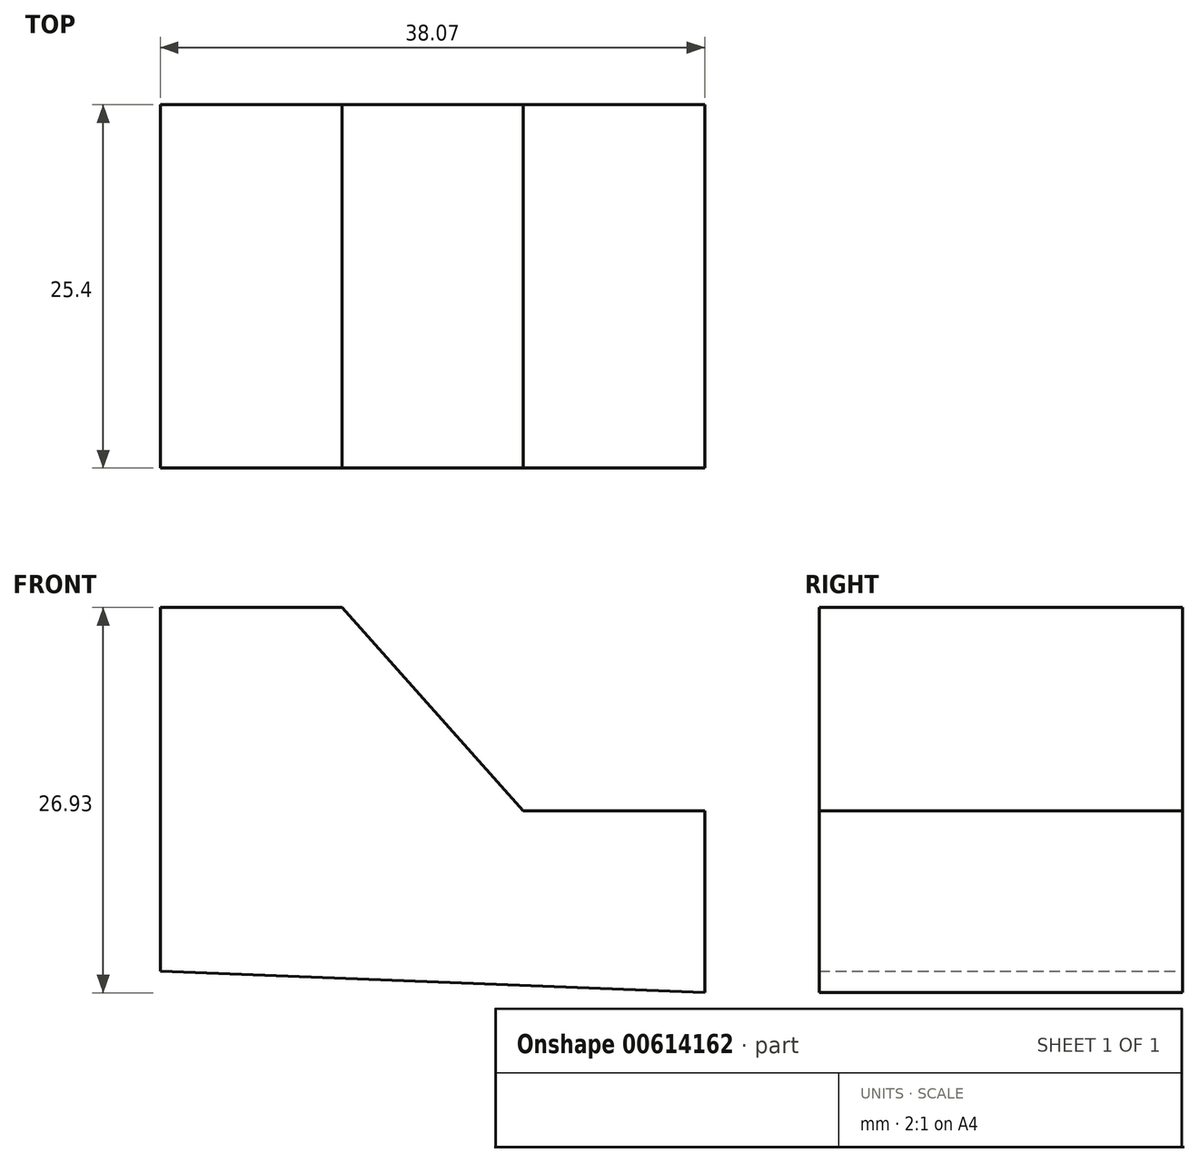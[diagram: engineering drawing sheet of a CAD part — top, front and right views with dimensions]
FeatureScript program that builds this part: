
annotation { "Feature Type Name" : "Feature", "Feature Type Description" : "" }
export const myFeature = defineFeature(function(context is Context, id is Id, definition is map)
    precondition{}
    {
        {
            var Q0;
            Q0=qCreatedBy(makeId("Front.planeOp"),FACE);
            var sketch = newSketch(context, id + "F0", { "sketchPlane" : qUnion([Q0])});
            skLineSegment(sketch, "E0", {"start": v(0, 0) * mm, "end": v(0, 38.1) * mm});
            skLineSegment(sketch, "E1", {"start": v(0, 38.1) * mm, "end": v(12.7, 38.1) * mm});
            skLineSegment(sketch, "E2", {"start": v(12.7, 38.1) * mm, "end": v(25.37, 23.87) * mm});
            skLineSegment(sketch, "E3", {"start": v(25.37, 23.87) * mm, "end": v(38.07, 23.87) * mm});
            skLineSegment(sketch, "E4", {"start": v(38.07, 23.87) * mm, "end": v(38.07, 11.17) * mm});
            skLineSegment(sketch, "E5", {"start": v(38.07, 11.17) * mm, "end": v(0, 12.69) * mm});
            skSolve(sketch);
        }
        {
            var Q0;
            {var subQ0=sQuery(id+"F0.wireOp",EDGE,"E1");Q0=makeQuery(id+"F0.imprint","IMPRINT",FACE,{"disambiguationData":[TD([[makeQuery(id+"F0.imprint","IMPRINT",EDGE,{"derivedFrom":subQ0}),-1.0]])]});}
            extrude(context, id + "F1", {"entities" : qUnion([Q0]), "depth" : 25.4 * mm, "offsetDistance" : 25.4 * mm});
        }
    });
